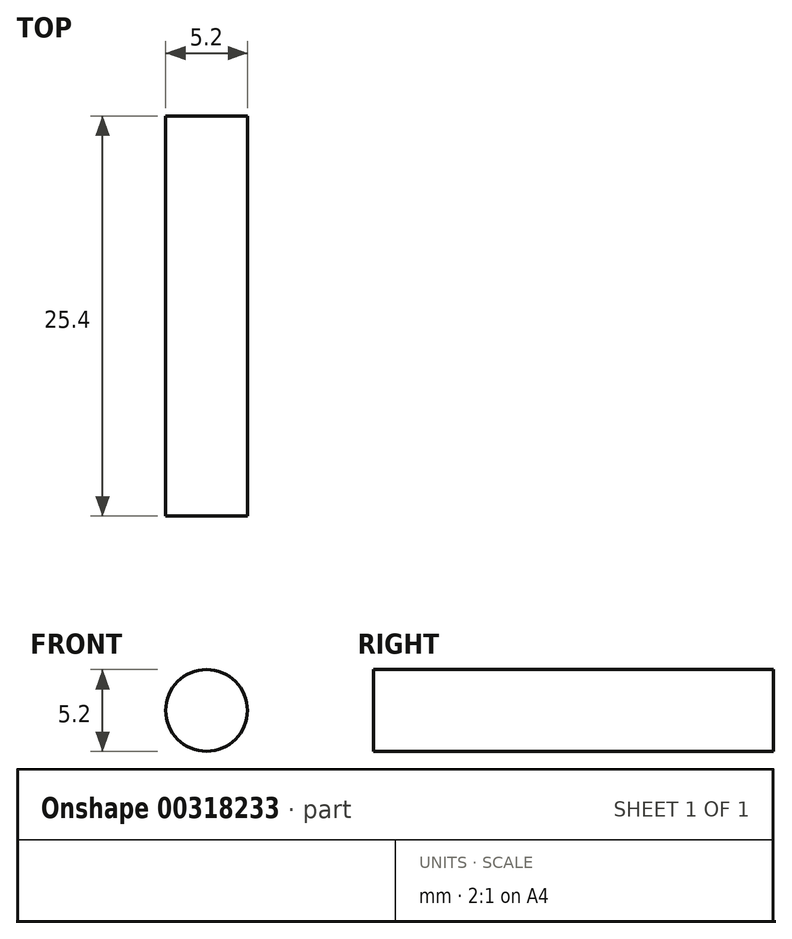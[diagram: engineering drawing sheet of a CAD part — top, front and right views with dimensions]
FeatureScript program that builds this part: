
annotation { "Feature Type Name" : "Feature", "Feature Type Description" : "" }
export const myFeature = defineFeature(function(context is Context, id is Id, definition is map)
    precondition{}
    {
        {
            var Q0;
            Q0=qCreatedBy(makeId("Front.planeOp"),FACE);
            var sketch = newSketch(context, id + "F0", { "sketchPlane" : qUnion([Q0])});
            skCircle(sketch, "E0", {"center": v(0, 0) * mm, "radius": 2.6 * mm});
            skSolve(sketch);
        }
        {
            var Q0;
            Q0 = qSketchRegion(id + "F0", true);
            extrude(context, id + "F1", {"entities" : qUnion([Q0]), "depth" : 25.4 * mm});
        }
    });
